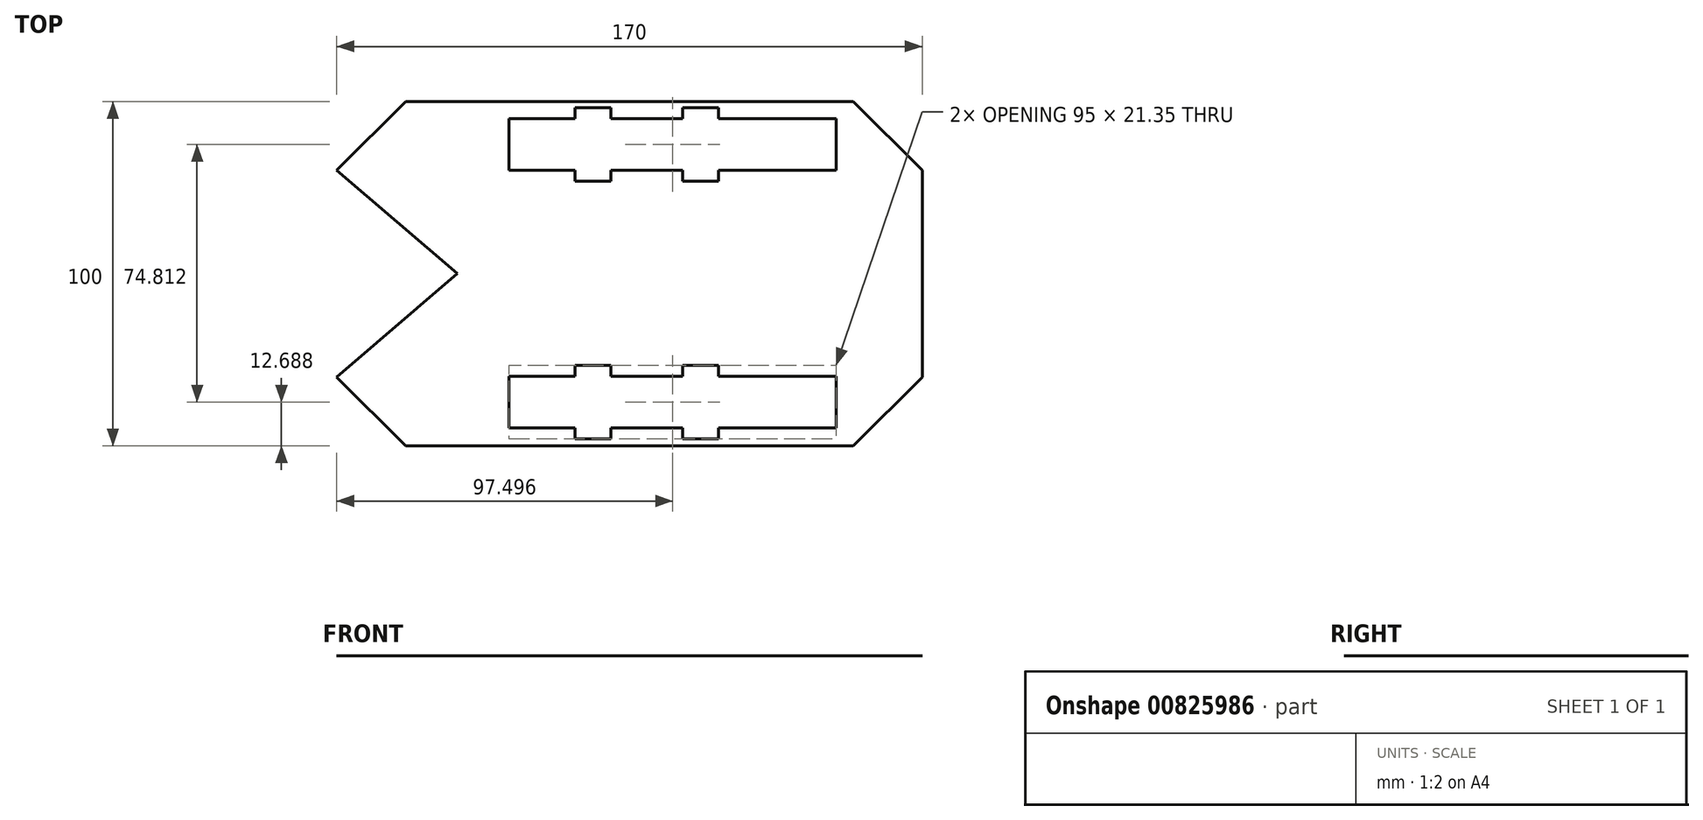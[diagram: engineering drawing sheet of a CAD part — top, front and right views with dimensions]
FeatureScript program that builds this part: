
annotation { "Feature Type Name" : "Feature", "Feature Type Description" : "" }
export const myFeature = defineFeature(function(context is Context, id is Id, definition is map)
    precondition{}
    {
        {
            var Q0;
            Q0=qCreatedBy(makeId("Top.planeOp"),FACE);
            var sketch = newSketch(context, id + "F0", { "sketchPlane" : qUnion([Q0])});
            skLineSegment(sketch, "E0.bottom", {"start": v(-45.53, 81.87) * mm, "end": v(84.47, 81.87) * mm});
            skLineSegment(sketch, "E0.top", {"start": v(-45.53, -18.13) * mm, "end": v(84.47, -18.13) * mm});
            skLineSegment(sketch, "E0.right", {"start": v(104.47, 61.87) * mm, "end": v(104.47, 1.87) * mm});
            skLineSegment(sketch, "E1", {"start": v(104.47, 61.87) * mm, "end": v(84.47, 81.87) * mm});
            skLineSegment(sketch, "E2", {"start": v(104.47, 1.87) * mm, "end": v(84.47, -18.13) * mm});
            skLineSegment(sketch, "E3", {"start": v(-45.53, -18.13) * mm, "end": v(-65.53, 1.87) * mm});
            skLineSegment(sketch, "E4", {"start": v(-65.53, 61.87) * mm, "end": v(-45.53, 81.87) * mm});
            skPoint(sketch, "E5.orphan", {"position": v(104.47, -18.13) * mm});
            skPoint(sketch, "E6.orphan", {"position": v(104.47, 81.87) * mm});
            skPoint(sketch, "E7.orphan", {"position": v(-65.53, 81.87) * mm});
            skPoint(sketch, "E8.start.orphan", {"position": v(104.47, 31.87) * mm});
            skLineSegment(sketch, "E9.bottom", {"start": v(-15.53, 2.06) * mm, "end": v(3.62, 2.06) * mm});
            skLineSegment(sketch, "E9.top", {"start": v(-15.53, -12.94) * mm, "end": v(3.62, -12.94) * mm});
            skLineSegment(sketch, "E9.left", {"start": v(-15.53, 2.06) * mm, "end": v(-15.53, -12.94) * mm});
            skLineSegment(sketch, "E10.bottom", {"start": v(-15.53, 76.87) * mm, "end": v(3.62, 76.87) * mm});
            skLineSegment(sketch, "E10.top", {"start": v(-15.53, 61.87) * mm, "end": v(3.62, 61.87) * mm});
            skLineSegment(sketch, "E10.left", {"start": v(-15.53, 76.87) * mm, "end": v(-15.53, 61.87) * mm});
            skPoint(sketch, "E11.top.start.orphan", {"position": v(-40.53, 4.37) * mm});
            skLineSegment(sketch, "E12", {"start": v(-30.53, 31.87) * mm, "end": v(-65.53, 61.87) * mm});
            skLineSegment(sketch, "E13", {"start": v(-30.53, 31.87) * mm, "end": v(-65.53, 1.87) * mm});
            skLineSegment(sketch, "E14.top", {"start": v(3.62, 58.7) * mm, "end": v(14.05, 58.7) * mm});
            skLineSegment(sketch, "E14.left", {"start": v(3.62, 61.87) * mm, "end": v(3.62, 58.7) * mm});
            skLineSegment(sketch, "E14.right", {"start": v(14.05, 61.87) * mm, "end": v(14.05, 58.7) * mm});
            skLineSegment(sketch, "E15.top", {"start": v(34.88, 58.7) * mm, "end": v(45.3, 58.7) * mm});
            skLineSegment(sketch, "E15.left", {"start": v(34.88, 61.87) * mm, "end": v(34.88, 58.7) * mm});
            skLineSegment(sketch, "E15.right", {"start": v(45.3, 62.06) * mm, "end": v(45.3, 58.7) * mm});
            skLineSegment(sketch, "E16.trimOffspring", {"start": v(45.3, 61.87) * mm, "end": v(64.47, 61.87) * mm});
            skLineSegment(sketch, "E17", {"start": v(14.05, 61.87) * mm, "end": v(34.88, 61.87) * mm});
            skLineSegment(sketch, "E18.top", {"start": v(3.62, 80.05) * mm, "end": v(14.05, 80.05) * mm});
            skLineSegment(sketch, "E18.left", {"start": v(3.62, 76.87) * mm, "end": v(3.62, 80.05) * mm});
            skLineSegment(sketch, "E18.right", {"start": v(14.05, 76.87) * mm, "end": v(14.05, 80.05) * mm});
            skLineSegment(sketch, "E19.top", {"start": v(34.88, 80.05) * mm, "end": v(45.3, 80.05) * mm});
            skLineSegment(sketch, "E19.left", {"start": v(34.88, 76.87) * mm, "end": v(34.88, 80.05) * mm});
            skLineSegment(sketch, "E19.right", {"start": v(45.3, 76.87) * mm, "end": v(45.3, 80.05) * mm});
            skLineSegment(sketch, "E20.trimOffspring", {"start": v(14.05, 76.87) * mm, "end": v(34.88, 76.87) * mm});
            skLineSegment(sketch, "E21.trimOffspring", {"start": v(45.3, 76.87) * mm, "end": v(64.47, 76.87) * mm});
            skLineSegment(sketch, "E22.top", {"start": v(3.62, 5.23) * mm, "end": v(14.05, 5.23) * mm});
            skLineSegment(sketch, "E22.left", {"start": v(3.62, 2.06) * mm, "end": v(3.62, 5.23) * mm});
            skLineSegment(sketch, "E22.right", {"start": v(14.05, 2.06) * mm, "end": v(14.05, 5.23) * mm});
            skLineSegment(sketch, "E23.top", {"start": v(34.88, 5.23) * mm, "end": v(45.3, 5.23) * mm});
            skLineSegment(sketch, "E23.left", {"start": v(34.88, 2.06) * mm, "end": v(34.88, 5.23) * mm});
            skLineSegment(sketch, "E23.right", {"start": v(45.3, 2.06) * mm, "end": v(45.3, 5.23) * mm});
            skLineSegment(sketch, "E24.top", {"start": v(3.62, -16.12) * mm, "end": v(14.05, -16.12) * mm});
            skLineSegment(sketch, "E24.left", {"start": v(3.62, -12.94) * mm, "end": v(3.62, -16.12) * mm});
            skLineSegment(sketch, "E24.right", {"start": v(14.05, -12.94) * mm, "end": v(14.05, -16.12) * mm});
            skLineSegment(sketch, "E25.top", {"start": v(34.88, -16.12) * mm, "end": v(45.3, -16.12) * mm});
            skLineSegment(sketch, "E25.left", {"start": v(34.88, -12.94) * mm, "end": v(34.88, -16.12) * mm});
            skLineSegment(sketch, "E25.right", {"start": v(45.3, -12.94) * mm, "end": v(45.3, -16.12) * mm});
            skLineSegment(sketch, "E26.trimOffspring", {"start": v(14.05, -12.94) * mm, "end": v(34.88, -12.94) * mm});
            skLineSegment(sketch, "E27.trimOffspring", {"start": v(14.05, 2.06) * mm, "end": v(34.88, 2.06) * mm});
            skLineSegment(sketch, "E28.trimOffspring", {"start": v(45.3, 2.06) * mm, "end": v(64.47, 2.06) * mm});
            skLineSegment(sketch, "E29.trimOffspring", {"start": v(45.3, -12.94) * mm, "end": v(64.47, -12.94) * mm});
            skLineSegment(sketch, "E30", {"start": v(64.47, 2.06) * mm, "end": v(74.47, 2.06) * mm});
            skLineSegment(sketch, "E31", {"start": v(74.47, 2.06) * mm, "end": v(74.47, -12.94) * mm});
            skLineSegment(sketch, "E32", {"start": v(64.47, -12.94) * mm, "end": v(74.47, -12.94) * mm});
            skLineSegment(sketch, "E33", {"start": v(64.47, 76.87) * mm, "end": v(74.47, 76.87) * mm});
            skLineSegment(sketch, "E34", {"start": v(74.47, 76.87) * mm, "end": v(74.47, 61.87) * mm});
            skLineSegment(sketch, "E35", {"start": v(64.47, 61.87) * mm, "end": v(74.47, 61.87) * mm});
            skLineSegment(sketch, "E36.bottom", {"start": v(74.47, 76.87) * mm, "end": v(79.47, 76.87) * mm});
            skLineSegment(sketch, "E36.top", {"start": v(74.47, 61.87) * mm, "end": v(79.47, 61.87) * mm});
            skLineSegment(sketch, "E36.right", {"start": v(79.47, 76.87) * mm, "end": v(79.47, 61.87) * mm});
            skLineSegment(sketch, "E37.bottom", {"start": v(74.47, 2.06) * mm, "end": v(79.47, 2.06) * mm});
            skLineSegment(sketch, "E37.top", {"start": v(74.47, -12.94) * mm, "end": v(79.47, -12.94) * mm});
            skLineSegment(sketch, "E37.right", {"start": v(79.47, 2.06) * mm, "end": v(79.47, -12.94) * mm});
            skSolve(sketch);
        }
        {
            var Q0;
            Q0=qSketchRegion(id+"F0",true);
            extrude(context, id + "F1", {"entities" : qUnion([Q0]), "depth" : 1 / 203.2 * mm, "offsetDistance" : 25.4 * mm});
        }
    });
